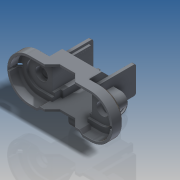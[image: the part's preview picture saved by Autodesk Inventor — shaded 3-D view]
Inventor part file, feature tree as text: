
AUTODESK INVENTOR PART (.ipt)
format: ipt  version: 2016 SP2 (Build 200236200, 236)  size: 1,150,464 bytes
history: native  units: in
note: dims shown in document units (in); Inventor stores cm internally (conversion verified against a paired STEP export)
features: extrude x24, sketch x5, chamfer x3, fillet x2, projected_geometry x1
ambient origin geometry x8: Origin, YZ Plane, XZ Plane, XY Plane, X Axis, Y Axis, Z Axis, Center Point
bodies: Solid1 (feature_tree)
feature tree (35):
  sketch  "Sketch2"  dims[d0=0.8119in d1=0.9134in d2=1.2598in]
  extrude  "Extrusion1"  Depth=0.9134in
  extrude  "Extrusion2"  Depth=0.9134in
  extrude  "Extrusion3"  Depth=0.9449in
  extrude  "Extrusion4"  Depth=0.189in
  extrude  "Extrusion5"  Depth=0.0157in
  extrude  "Extrusion6"  Depth=0.0157in TaperAngle=0.0deg
  extrude  "Extrusion7"  Depth=0.252in TaperAngle=0.0deg
  sketch  "Sketch3"  dims[d3=0.8119in d5=0.9134in]
  extrude  "Extrusion8"  Depth=0.0157in
  extrude  "Extrusion9"  Depth=0.063in
  extrude  "Extrusion10"  Depth=0.0157in
  extrude  "Extrusion11"  Depth=0.2835in
  extrude  "Extrusion12"  Depth=0.063in
  sketch  "Sketch4"  dims[d6=0.8189in d7=0.9449in]
  extrude  "Extrusion23"  TaperAngle=0.0deg  [1 undecoded]
  extrude  "Extrusion16"  Depth=0.0157in
  extrude  "Extrusion17"  TaperAngle=0.0deg  [1 undecoded]
  extrude  "Extrusion18"  Depth=0.0945in TaperAngle=0.0deg
  extrude  "Extrusion19"  Depth=0.0157in TaperAngle=0.0deg
  extrude  "Extrusion24"  Depth=0.0157in
  extrude  "Extrusion20"  Depth=0.063in
  extrude  "Extrusion22"  Depth=0.0945in
  extrude  "Extrusion25"  Depth=0.0157in TaperAngle=0.0deg
  extrude  "Extrusion26"  Depth=0.063in
  chamfer  "Chamfer1"  Distance=0.8504in
  chamfer  "Chamfer4"  Distance=0.0157in
  chamfer  "Chamfer3"  Distance=0.2835in
  fillet  "Fillet1"  Radius=0.2441in
  sketch  "Sketch6"  dims[d12=0.252in d13=0.7244in d14=0.0472in d15=0.0in d16=0.252in d17=0.0in d18=0.9449in d19=0.063in d20=0.6299in d22=0.2835in d23=0.063in d24=0.0in d25=0.378in d26=0.0in d27=0.0945in d28=0.0in d29=0.8504in d30=0.0in d31=2.1417in d32=0.063in d33=0.0945in d34=0.8504in d35=0.0in d36=0.063in d38=0.8504in d39=0.0in d40=0.0157in d41=0.2835in d42=0.2441in d43=0.189in d45=0.315in d47=0.0472in d48=0.0472in d49=45.0deg d50=0.063in d51=0.2205in d52=0.0472in d53=0.0472in d54=0.063in d55=0.0in d56=0.252in d57=0.0in d58=0.315in d59=0.0in d60=0.0787in d65=0.7559in d66=0.2362in d67=0.8189in d68=0.0in d71=0.1417in d72=0.063in d73=0.1102in d75=0.063in d78=0.0472in d79=0.1417in d85=0.0472in d86=0.0472in d87=0.2992in d90=0.6299in d91=0.0in d92=0.0472in d93=0.0in d94=0.7244in d95=0.0in d96=0.7559in d97=0.6299in d99=0.7244in d100=0.0in d101=0.063in d102=0.0in d105=0.2441in d106=0.0315in d107=0.0in d110=0.0787in d111=0.0315in d112=0.0in d113=0.1732in d114=0.0in d115=0.0472in d116=0.0945in d119=0.3622in d120=0.3937in d122=135.0deg d123=0.7244in d124=0.0in d125=0.7244in d126=0.0in d127=0.063in d128=0.0787in d129=0.3023in d133=0.0315in d134=0.0787in d135=0.29in d136=0.0472in d137=0.063in d138=0.0787in d139=0.3023in d140=0.6299in d141=0.315in d142=0.1575in d143=0.7244in d144=0.0in d145=0.1417in d146=0.0472in d147=0.0315in d148=0.063in d149=0.0in d150=0.0039in d151=0.0157in]
  extrude  "Extrusion27"  Depth=0.189in
  extrude  "Extrusion28"  Depth=0.315in
  fillet  "Fillet2"  Radius=0.0472in
  sketch  "Sketch5"  dims[d10=0.5354in d11=0.189in]
  projected_geometry  "Projected Loop1"
note: 2 required parameter values undecoded (feature->parameter linkage not recoverable at this tier; creation-order binding heuristic only, values carry confidence <= 0.55)
